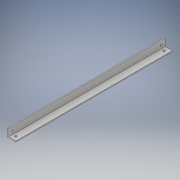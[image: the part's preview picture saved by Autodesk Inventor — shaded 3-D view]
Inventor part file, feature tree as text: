
AUTODESK INVENTOR PART (.ipt)
format: ipt  version: 2017 (Build 210142000, 142)  size: 122,880 bytes
history: native  units: in
note: dims shown in document units (in); Inventor stores cm internally (conversion verified against a paired STEP export)
features: hole x2, sketch x2, extrude x1
ambient origin geometry x8: Origin, YZ Plane, XZ Plane, XY Plane, X Axis, Y Axis, Z Axis, Center Point
bodies: Solid1 (feature_tree)
feature tree (5):
  extrude  "Extrusion1"  Depth=1.0in
  hole  "Hole1"  [1 undecoded]
  hole  "Hole4"  [1 undecoded]
  sketch  "Sketch2"  dims[d0=1.0in d1=1.0in]
  sketch  "Sketch7"  dims[d2=0.125in d3=19.375in d4=0.0in d5=0.5in d6=0.5in d7=0.7874in d9=18.375in d10=0.3937in d12=1.0in d14=0.266in d15=0.75in d16=0.385in d17=0.25in d18=0.5635in d19=1.0in d20=0.8108in d31=0.5in d43=0.5in d44=0.5in d45=0.7874in d47=18.375in d48=0.3937in d50=1.0in d52=0.266in d53=0.75in d54=0.507in d55=0.25in d56=0.5635in d57=1.0in d58=0.8108in]
note: 2 required parameter values undecoded (feature->parameter linkage not recoverable at this tier; creation-order binding heuristic only, values carry confidence <= 0.55)
